# Revit family: GC - Montante Laterale
name_source: partatom
category: Generic Models
revit_build: Autodesk Revit 2018 (Build: 20170223_1515(x64)
units: mm (PartAtom-declared; Revit-internal decimal feet)

## family parameters
Can host rebar = No
Cut with Voids When Loaded = No
Host = Face
Part Type = Normal
Room Calculation Point = No
Round Connector Dimension = Use Diameter
Shared = No

## types (1)
- GC - Montante Laterale
    Default Elevation = 121.92 cm
    Montante _ Altezza = 10.00 cm
    Montante _ Diametro Foro = 1.00 cm
    Montante _ Distanza Fori = 15.00 cm
    Montante _ Larghezza Piatto = 10.00 cm
    Montante _ Lunghezza = 300.00 cm
    Montante _ Posizionamento Fori = 30.00 cm
    Montante _ Posizione Foro Ala = 2.25 cm
    Montante _ Posizione Foro Anima Inferiore = 3.50 cm
    Montante _ Posizione Foro Anima Superiore = 2.50 cm
    Montante _ Raggio Foro = 0.50 cm
    Montante _ Spessore = 1.00 cm

## geometry (parser evidence)
native form markers: Sweep x3
no freeform markers — native parametric forms only
